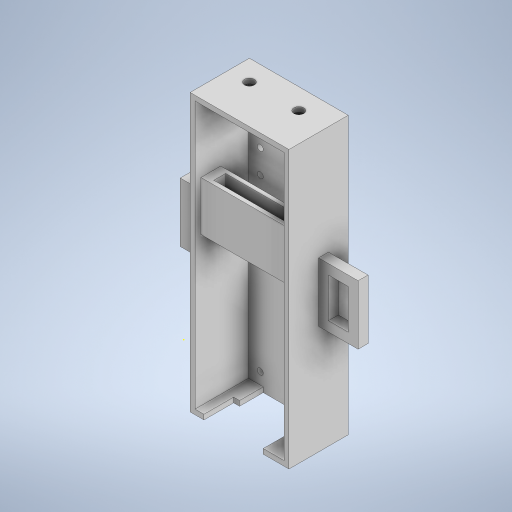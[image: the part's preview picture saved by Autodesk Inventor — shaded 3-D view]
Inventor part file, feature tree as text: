
AUTODESK INVENTOR PART (.ipt)
format: ipt  version: 2023 (Build 270158000, 158)  size: 375,296 bytes
history: native  units: mm
features: sketch x9, extrude x8, plane x2
ambient origin geometry x8: Origin, YZ Plane, XZ Plane, XY Plane, X Axis, Y Axis, Z Axis, Center Point
bodies: Solid1 (feature_tree)
feature tree (19):
  extrude  "Extrusion1"  Depth=50.0mm
  extrude  "Extrusion2"  Depth=2.5mm
  extrude  "Extrusion3"  Depth=2.5mm
  extrude  "Extrusion4"  Depth=27.0mm TaperAngle=0.0deg
  extrude  "Extrusion5"  Depth=30.0mm
  sketch  "Sketch6"  dims[d12=7.0mm d13=0.0mm]
  plane  "Work Plane1"
  extrude  "Extrusion6"  TaperAngle=0.0deg  [1 undecoded]
  plane  "Work Plane2"
  extrude  "Extrusion7"  Depth=10.0mm
  extrude  "Extrusion8"  Depth=27.0mm TaperAngle=0.0deg
  sketch  "Sketch1"  dims[d0=140.0mm d1=50.0mm]
  sketch  "Sketch2"  dims[d2=30.0mm d3=0.0mm d4=2.5mm]
  sketch  "Sketch3"  dims[d5=2.5mm d6=2.5mm]
  sketch  "Sketch4"  dims[d7=2.5mm d8=27.0mm d9=0.0mm]
  sketch  "Sketch5"  dims[d10=15.0mm d11=30.0mm]
  sketch  "Sketch7"  dims[d14=25.0mm d15=10.0mm]
  sketch  "Sketch8"  dims[d16=3.0mm d17=27.0mm d18=0.0mm]
  sketch  "Sketch9"  dims[d19=8.5mm d20=8.5mm d21=8.5mm d22=8.5mm d23=3.0mm d24=3.0mm d25=8.5mm d26=8.5mm d27=8.5mm d28=8.5mm d29=3.0mm d30=3.0mm d31=3.0mm d32=3.0mm d33=12.0mm d34=12.0mm d35=33.5mm d36=33.5mm d37=27.0mm d38=0.0mm d39=5.0mm d40=5.0mm d41=25.0mm d42=14.5mm d43=10.5mm d44=10.5mm d45=27.0mm d46=0.0mm d55=-12.5mm d56=20.0mm d57=30.0mm d58=55.0mm d59=5.0mm d60=20.0mm d61=30.0mm d62=55.0mm d63=5.0mm d64=5.0mm d65=0.0mm d66=-3.0mm d67=35.0mm d68=25.0mm d69=10.0mm d70=0.0mm d72=2.0mm d73=2.0mm d74=2.0mm d75=2.0mm d76=27.0mm d77=0.0mm]
note: 1 required parameter value undecoded (feature->parameter linkage not recoverable at this tier; creation-order binding heuristic only, values carry confidence <= 0.55)
